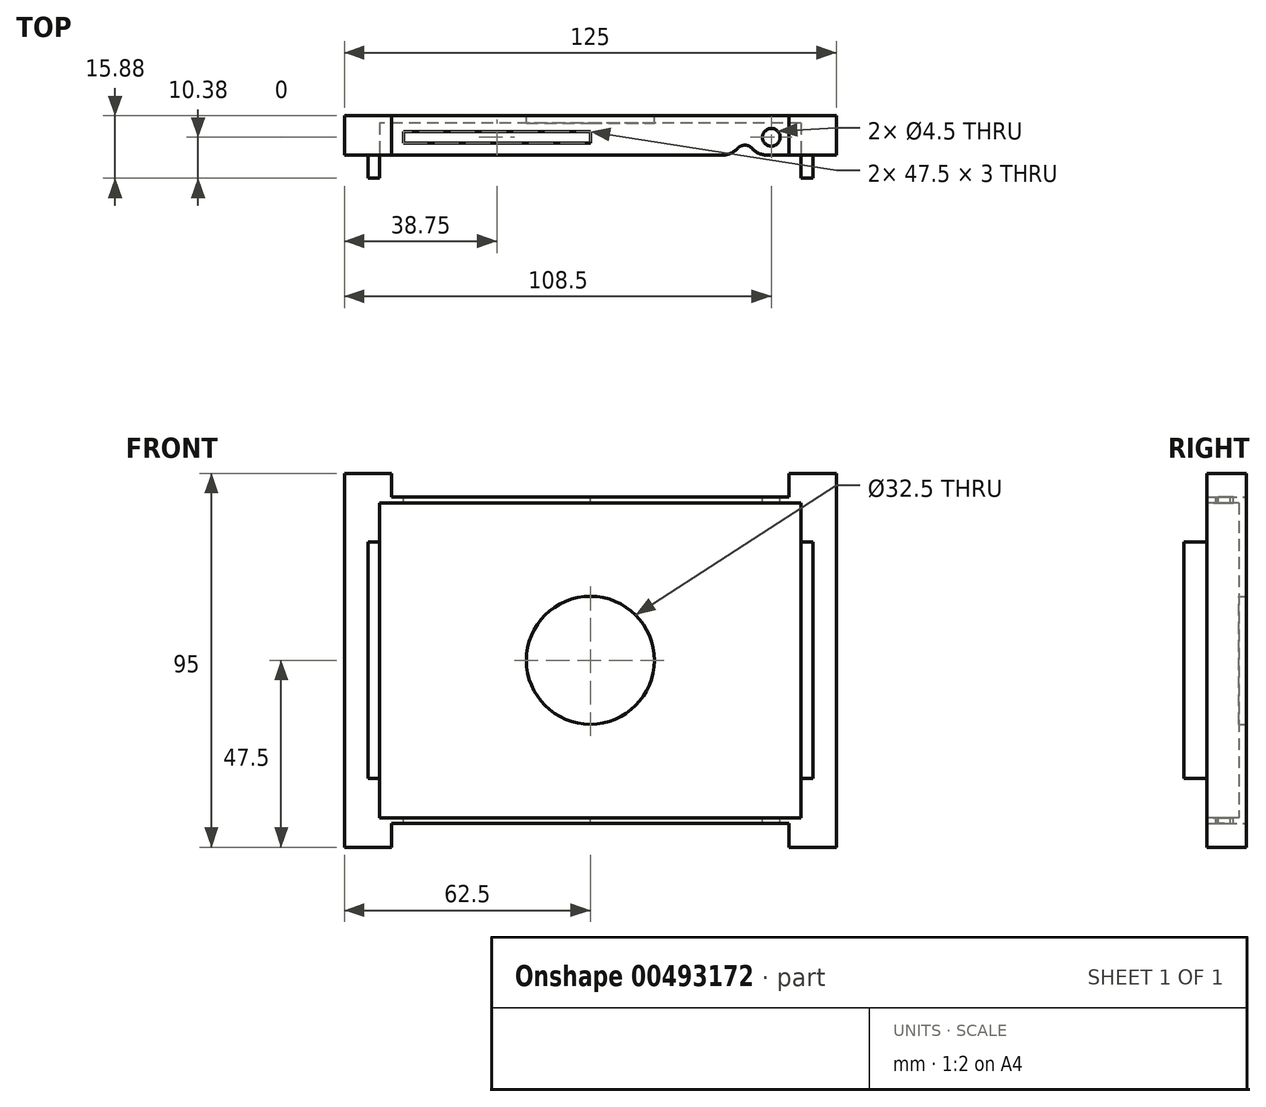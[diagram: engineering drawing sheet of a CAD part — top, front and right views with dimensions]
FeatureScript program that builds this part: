
annotation { "Feature Type Name" : "Feature", "Feature Type Description" : "" }
export const myFeature = defineFeature(function(context is Context, id is Id, definition is map)
    precondition{}
    {
        {
            var Q0;
            Q0=qCreatedBy(makeId("Front.planeOp"),FACE);
            var sketch = newSketch(context, id + "F0", { "sketchPlane" : qUnion([Q0])});
            skLineSegment(sketch, "E0.bottom", {"start": v(62.5, 47.5) * mm, "end": v(-62.5, 47.5) * mm, "construction": true});
            skLineSegment(sketch, "E0.top", {"start": v(62.5, -47.5) * mm, "end": v(-62.5, -47.5) * mm, "construction": true});
            skLineSegment(sketch, "E0.left", {"start": v(62.5, 47.5) * mm, "end": v(62.5, -47.5) * mm, "construction": true});
            skLineSegment(sketch, "E0.right", {"start": v(-62.5, 47.5) * mm, "end": v(-62.5, -47.5) * mm, "construction": true});
            skPoint(sketch, "E0.middle", {"position": v(0, 0) * mm});
            skLineSegment(sketch, "E1", {"start": v(-62.5, 47.5) * mm, "end": v(-50.5, 47.5) * mm});
            skLineSegment(sketch, "E2", {"start": v(62.5, 47.5) * mm, "end": v(50.5, 47.5) * mm});
            skLineSegment(sketch, "E3", {"start": v(50.5, 47.5) * mm, "end": v(50.5, 41.5) * mm});
            skLineSegment(sketch, "E4", {"start": v(50.5, 41.5) * mm, "end": v(-50.5, 41.5) * mm});
            skLineSegment(sketch, "E5", {"start": v(-50.5, 41.5) * mm, "end": v(-50.5, 47.5) * mm});
            skLineSegment(sketch, "E6", {"start": v(62.5, 47.5) * mm, "end": v(62.5, -47.5) * mm});
            skLineSegment(sketch, "E7", {"start": v(-62.5, -47.5) * mm, "end": v(-62.5, 47.5) * mm});
            skLineSegment(sketch, "E8", {"start": v(62.5, -47.5) * mm, "end": v(50.5, -47.5) * mm});
            skLineSegment(sketch, "E9", {"start": v(50.5, -47.5) * mm, "end": v(50.5, -41.5) * mm});
            skLineSegment(sketch, "E10", {"start": v(50.5, -41.5) * mm, "end": v(-50.5, -41.5) * mm});
            skLineSegment(sketch, "E11", {"start": v(-50.5, -41.5) * mm, "end": v(-50.5, -47.5) * mm});
            skLineSegment(sketch, "E12", {"start": v(-50.5, -47.5) * mm, "end": v(-62.5, -47.5) * mm});
            skCircle(sketch, "E13", {"center": v(0, 0) * mm, "radius": 16.25 * mm});
            skSolve(sketch);
        }
        {
            var Q0;
            Q0=qSketchRegion(id+"F0",true);
            extrude(context, id + "F1", {"entities" : qUnion([Q0]), "depth" : 15.88 * mm});
        }
        {
            var Q0;
            Q0=makeQuery(id+"F1.opExtrude","CAP_FACE",FACE,{"disambiguationData":[OSD([sQuery(id+"F0.wireOp",EDGE,"E1"),sQuery(id+"F0.wireOp",EDGE,"E2"),sQuery(id+"F0.wireOp",EDGE,"E3"),sQuery(id+"F0.wireOp",EDGE,"E4"),sQuery(id+"F0.wireOp",EDGE,"E5"),sQuery(id+"F0.wireOp",EDGE,"E6"),sQuery(id+"F0.wireOp",EDGE,"E7"),sQuery(id+"F0.wireOp",EDGE,"E8"),sQuery(id+"F0.wireOp",EDGE,"E9"),sQuery(id+"F0.wireOp",EDGE,"E10"),sQuery(id+"F0.wireOp",EDGE,"E11"),sQuery(id+"F0.wireOp",EDGE,"E12"),sQuery(id+"F0.wireOp",EDGE,"E13")])],"isStart":false});
            var sketch = newSketch(context, id + "F2", { "sketchPlane" : qUnion([Q0])});
            skLineSegment(sketch, "E14.bottom", {"start": v(56.5, 40) * mm, "end": v(-56.5, 40) * mm});
            skLineSegment(sketch, "E14.top", {"start": v(56.5, -40) * mm, "end": v(-56.5, -40) * mm});
            skLineSegment(sketch, "E14.left", {"start": v(56.5, 40) * mm, "end": v(56.5, -40) * mm});
            skLineSegment(sketch, "E14.right", {"start": v(-56.5, 40) * mm, "end": v(-56.5, -40) * mm});
            skPoint(sketch, "E14.middle", {"position": v(0, 0) * mm});
            skLineSegment(sketch, "E15.bottom", {"start": v(69.6, 57.77) * mm, "end": v(-69.6, 57.77) * mm});
            skLineSegment(sketch, "E15.top", {"start": v(69.6, -57.77) * mm, "end": v(-69.6, -57.77) * mm});
            skLineSegment(sketch, "E15.left", {"start": v(69.6, 57.77) * mm, "end": v(69.6, -57.77) * mm});
            skLineSegment(sketch, "E15.right", {"start": v(-69.6, 57.77) * mm, "end": v(-69.6, -57.77) * mm});
            skSolve(sketch);
        }
        {
            var Q0;
            Q0=qSketchRegion(id+"F2",true);
            extrude(context, id + "F3", {"entities" : qUnion([Q0]), "operationType" : NewBodyOperationType.REMOVE, "oppositeDirection" : true, "depth" : 5.88 * mm});
        }
        {
            var Q0;
            Q0=makeQuery(id+"F1.opExtrude","CAP_FACE",FACE,{"disambiguationData":[OSD([sQuery(id+"F0.wireOp",EDGE,"E1"),sQuery(id+"F0.wireOp",EDGE,"E2"),sQuery(id+"F0.wireOp",EDGE,"E3"),sQuery(id+"F0.wireOp",EDGE,"E4"),sQuery(id+"F0.wireOp",EDGE,"E5"),sQuery(id+"F0.wireOp",EDGE,"E6"),sQuery(id+"F0.wireOp",EDGE,"E7"),sQuery(id+"F0.wireOp",EDGE,"E8"),sQuery(id+"F0.wireOp",EDGE,"E9"),sQuery(id+"F0.wireOp",EDGE,"E10"),sQuery(id+"F0.wireOp",EDGE,"E11"),sQuery(id+"F0.wireOp",EDGE,"E12"),sQuery(id+"F0.wireOp",EDGE,"E13")])],"isStart":false});
            var sketch = newSketch(context, id + "F4", { "sketchPlane" : qUnion([Q0])});
            skLineSegment(sketch, "E16.bottom", {"start": v(53.5, 40) * mm, "end": v(-53.5, 40) * mm});
            skLineSegment(sketch, "E16.top", {"start": v(53.5, -40) * mm, "end": v(-53.5, -40) * mm});
            skLineSegment(sketch, "E16.left", {"start": v(53.5, 40) * mm, "end": v(53.5, -40) * mm});
            skLineSegment(sketch, "E16.right", {"start": v(-53.5, 40) * mm, "end": v(-53.5, -40) * mm});
            skPoint(sketch, "E16.middle", {"position": v(0, 0) * mm});
            skSolve(sketch);
        }
        {
            var Q0;
            Q0=qSketchRegion(id+"F4",true);
            extrude(context, id + "F5", {"entities" : qUnion([Q0]), "operationType" : NewBodyOperationType.REMOVE, "oppositeDirection" : true, "depth" : 14 * mm});
        }
        {
            var Q0;
            Q0=makeQuery(id+"F5.boolean.opBoolean","SPLIT",FACE,{"disambiguationData":[TD([makeQuery(id+"F3.boolean.opBoolean","COPY",FACE,{"derivedFrom":makeQuery(id+"F3.opExtrude","SWEPT_FACE",FACE,{"disambiguationData":[OSD([sQuery(id+"F2.wireOp",EDGE,"E14.right")])]})})])],"derivedFrom":makeQuery(id+"F1.opExtrude","CAP_FACE",FACE,{"disambiguationData":[OSD([sQuery(id+"F0.wireOp",EDGE,"E1"),sQuery(id+"F0.wireOp",EDGE,"E2"),sQuery(id+"F0.wireOp",EDGE,"E3"),sQuery(id+"F0.wireOp",EDGE,"E4"),sQuery(id+"F0.wireOp",EDGE,"E5"),sQuery(id+"F0.wireOp",EDGE,"E6"),sQuery(id+"F0.wireOp",EDGE,"E7"),sQuery(id+"F0.wireOp",EDGE,"E8"),sQuery(id+"F0.wireOp",EDGE,"E9"),sQuery(id+"F0.wireOp",EDGE,"E10"),sQuery(id+"F0.wireOp",EDGE,"E11"),sQuery(id+"F0.wireOp",EDGE,"E12"),sQuery(id+"F0.wireOp",EDGE,"E13")])],"isStart":false})});
            var sketch = newSketch(context, id + "F6", { "sketchPlane" : qUnion([Q0])});
            skLineSegment(sketch, "E17.bottom", {"start": v(-60.23, 43.15) * mm, "end": v(60.36, 43.15) * mm});
            skLineSegment(sketch, "E17.top", {"start": v(-60.23, 30) * mm, "end": v(60.36, 30) * mm});
            skLineSegment(sketch, "E17.left", {"start": v(-60.23, 43.15) * mm, "end": v(-60.23, 30) * mm});
            skLineSegment(sketch, "E17.right", {"start": v(60.36, 43.15) * mm, "end": v(60.36, 30) * mm});
            skLineSegment(sketch, "E18.bottom", {"start": v(-59.64, -45.81) * mm, "end": v(61.69, -45.81) * mm});
            skLineSegment(sketch, "E18.top", {"start": v(-59.64, -30) * mm, "end": v(61.69, -30) * mm});
            skLineSegment(sketch, "E18.left", {"start": v(-59.64, -45.81) * mm, "end": v(-59.64, -30) * mm});
            skLineSegment(sketch, "E18.right", {"start": v(61.69, -45.81) * mm, "end": v(61.69, -30) * mm});
            skSolve(sketch);
        }
        {
            var Q0;
            Q0=qSketchRegion(id+"F6",true);
            extrude(context, id + "F7", {"entities" : qUnion([Q0]), "operationType" : NewBodyOperationType.REMOVE, "oppositeDirection" : true, "depth" : 5.88 * mm});
        }
        {
            var Q0;
            Q0=makeQuery(id+"F1.opExtrude","SWEPT_FACE",FACE,{"disambiguationData":[OSD([sQuery(id+"F0.wireOp",EDGE,"E4")])]});
            var sketch = newSketch(context, id + "F8", { "sketchPlane" : qUnion([Q0])});
            skCircle(sketch, "E19", {"center": v(46, -5.5) * mm, "radius": 1.5 * mm});
            skLineSegment(sketch, "E20.bottom", {"start": v(41.5, -4) * mm, "end": v(-47.5, -4) * mm});
            skLineSegment(sketch, "E20.top", {"start": v(41.5, -7) * mm, "end": v(-47.5, -7) * mm});
            skLineSegment(sketch, "E20.left", {"start": v(41.5, -4) * mm, "end": v(41.5, -7) * mm});
            skLineSegment(sketch, "E20.right", {"start": v(-47.5, -4) * mm, "end": v(-47.5, -7) * mm});
            skSolve(sketch);
        }
        {
            var Q0;
            Q0=qSketchRegion(id+"F8",true);
            extrude(context, id + "F9", {"entities" : qUnion([Q0]), "operationType" : NewBodyOperationType.REMOVE, "oppositeDirection" : true, "depth" : 100 * mm});
        }
        {
            var Q0;
            Q0=makeQuery(id+"F1.opExtrude","SWEPT_FACE",FACE,{"disambiguationData":[OSD([sQuery(id+"F0.wireOp",EDGE,"E4")])]});
            var sketch = newSketch(context, id + "F10", { "sketchPlane" : qUnion([Q0])});
            skLineSegment(sketch, "E21.bottom", {"start": v(0, 0) * mm, "end": v(42.44, 0) * mm});
            skLineSegment(sketch, "E21.top", {"start": v(0, -10) * mm, "end": v(42.44, -10) * mm});
            skLineSegment(sketch, "E21.left", {"start": v(0, 0) * mm, "end": v(0, -10) * mm});
            skLineSegment(sketch, "E21.right", {"start": v(42.44, 0) * mm, "end": v(42.44, -10) * mm});
            skSolve(sketch);
        }
        {
            var Q0;
            Q0=qSketchRegion(id+"F10",true);
            extrude(context, id + "F11", {"entities" : qUnion([Q0]), "operationType" : NewBodyOperationType.ADD, "oppositeDirection" : true, "depth" : 1.5 * mm});
        }
        {
            var Q0;
            Q0=makeQuery(id+"F1.opExtrude","SWEPT_FACE",FACE,{"disambiguationData":[OSD([sQuery(id+"F0.wireOp",EDGE,"E10")])]});
            var sketch = newSketch(context, id + "F12", { "sketchPlane" : qUnion([Q0])});
            skLineSegment(sketch, "E22.bottom", {"start": v(0, 10) * mm, "end": v(42.52, 10) * mm});
            skLineSegment(sketch, "E22.top", {"start": v(0, 0) * mm, "end": v(42.52, 0) * mm});
            skLineSegment(sketch, "E22.left", {"start": v(0, 10) * mm, "end": v(0, 0) * mm});
            skLineSegment(sketch, "E22.right", {"start": v(42.52, 10) * mm, "end": v(42.52, 0) * mm});
            skSolve(sketch);
        }
        {
            var Q0;
            Q0=qSketchRegion(id+"F12",true);
            extrude(context, id + "F13", {"entities" : qUnion([Q0]), "operationType" : NewBodyOperationType.ADD, "oppositeDirection" : true, "depth" : 1.5 * mm});
        }
        {
            var Q0;
            Q0=makeQuery(id+"F13.boolean.opBoolean","MERGE",FACE,{"derivedFrom":[makeQuery(id+"F1.opExtrude","SWEPT_FACE",FACE,{"disambiguationData":[OSD([sQuery(id+"F0.wireOp",EDGE,"E10")])]}),makeQuery(id+"F13.opExtrude","CAP_FACE",FACE,{"disambiguationData":[OSD([sQuery(id+"F12.wireOp",EDGE,"E22.bottom"),sQuery(id+"F12.wireOp",EDGE,"E22.top"),sQuery(id+"F12.wireOp",EDGE,"E22.left"),sQuery(id+"F12.wireOp",EDGE,"E22.right")])],"isStart":true})]});
            var sketch = newSketch(context, id + "F14", { "sketchPlane" : qUnion([Q0])});
            skCircle(sketch, "E23", {"center": v(39.25, 10) * mm, "radius": 2.5 * mm});
            skSolve(sketch);
        }
        {
            var Q0;
            Q0=qSketchRegion(id+"F14",true);
            extrude(context, id + "F15", {"entities" : qUnion([Q0]), "operationType" : NewBodyOperationType.REMOVE, "oppositeDirection" : true, "depth" : 95.5 * mm});
        }
        {
            var Q0;
            Q0=makeQuery(id+"F11.boolean.opBoolean","MERGE",FACE,{"derivedFrom":[makeQuery(id+"F1.opExtrude","SWEPT_FACE",FACE,{"disambiguationData":[OSD([sQuery(id+"F0.wireOp",EDGE,"E4")])]}),makeQuery(id+"F11.opExtrude","CAP_FACE",FACE,{"disambiguationData":[OSD([sQuery(id+"F10.wireOp",EDGE,"E21.bottom"),sQuery(id+"F10.wireOp",EDGE,"E21.top"),sQuery(id+"F10.wireOp",EDGE,"E21.left"),sQuery(id+"F10.wireOp",EDGE,"E21.right")])],"isStart":true})]});
            var sketch = newSketch(context, id + "F16", { "sketchPlane" : qUnion([Q0])});
            skCircle(sketch, "E24", {"center": v(46, -5.5) * mm, "radius": 2.25 * mm});
            skSolve(sketch);
        }
        {
            var Q0;
            Q0=qSketchRegion(id+"F16",true);
            extrude(context, id + "F17", {"entities" : qUnion([Q0]), "operationType" : NewBodyOperationType.REMOVE, "oppositeDirection" : true, "depth" : 200 * mm});
        }
        {
            var Q0;
            Q0=makeQuery(id+"F15.boolean.opBoolean","INTERSECT",EDGE,{"disambiguationData":[OD(3.0)],"derivedFrom":[makeQuery(id+"F7.boolean.opBoolean","MERGE",FACE,{"derivedFrom":[makeQuery(id+"F3.boolean.opBoolean","COPY",FACE,{"derivedFrom":makeQuery(id+"F3.opExtrude","CAP_FACE",FACE,{"disambiguationData":[OSD([sQuery(id+"F2.wireOp",EDGE,"E14.bottom"),sQuery(id+"F2.wireOp",EDGE,"E14.top"),sQuery(id+"F2.wireOp",EDGE,"E14.left"),sQuery(id+"F2.wireOp",EDGE,"E14.right"),sQuery(id+"F2.wireOp",EDGE,"E15.bottom"),sQuery(id+"F2.wireOp",EDGE,"E15.top"),sQuery(id+"F2.wireOp",EDGE,"E15.left"),sQuery(id+"F2.wireOp",EDGE,"E15.right")])],"isStart":false})}),makeQuery(id+"F7.opExtrude","CAP_FACE",FACE,{"disambiguationData":[OSD([sQuery(id+"F6.wireOp",EDGE,"E17.bottom"),sQuery(id+"F6.wireOp",EDGE,"E17.top"),sQuery(id+"F6.wireOp",EDGE,"E17.left"),sQuery(id+"F6.wireOp",EDGE,"E17.right")])],"isStart":false}),makeQuery(id+"F7.opExtrude","CAP_FACE",FACE,{"disambiguationData":[OSD([sQuery(id+"F6.wireOp",EDGE,"E18.bottom"),sQuery(id+"F6.wireOp",EDGE,"E18.top"),sQuery(id+"F6.wireOp",EDGE,"E18.left"),sQuery(id+"F6.wireOp",EDGE,"E18.right")])],"isStart":false})]}),makeQuery(id+"F15.opExtrude","SWEPT_FACE",FACE,{"disambiguationData":[OSD([sQuery(id+"F14.wireOp",EDGE,"E23")])]})]});
            var Q1;
            Q1=makeQuery(id+"F15.boolean.opBoolean","INTERSECT",EDGE,{"disambiguationData":[OD(2.0)],"derivedFrom":[makeQuery(id+"F7.boolean.opBoolean","MERGE",FACE,{"derivedFrom":[makeQuery(id+"F3.boolean.opBoolean","COPY",FACE,{"derivedFrom":makeQuery(id+"F3.opExtrude","CAP_FACE",FACE,{"disambiguationData":[OSD([sQuery(id+"F2.wireOp",EDGE,"E14.bottom"),sQuery(id+"F2.wireOp",EDGE,"E14.top"),sQuery(id+"F2.wireOp",EDGE,"E14.left"),sQuery(id+"F2.wireOp",EDGE,"E14.right"),sQuery(id+"F2.wireOp",EDGE,"E15.bottom"),sQuery(id+"F2.wireOp",EDGE,"E15.top"),sQuery(id+"F2.wireOp",EDGE,"E15.left"),sQuery(id+"F2.wireOp",EDGE,"E15.right")])],"isStart":false})}),makeQuery(id+"F7.opExtrude","CAP_FACE",FACE,{"disambiguationData":[OSD([sQuery(id+"F6.wireOp",EDGE,"E17.bottom"),sQuery(id+"F6.wireOp",EDGE,"E17.top"),sQuery(id+"F6.wireOp",EDGE,"E17.left"),sQuery(id+"F6.wireOp",EDGE,"E17.right")])],"isStart":false}),makeQuery(id+"F7.opExtrude","CAP_FACE",FACE,{"disambiguationData":[OSD([sQuery(id+"F6.wireOp",EDGE,"E18.bottom"),sQuery(id+"F6.wireOp",EDGE,"E18.top"),sQuery(id+"F6.wireOp",EDGE,"E18.left"),sQuery(id+"F6.wireOp",EDGE,"E18.right")])],"isStart":false})]}),makeQuery(id+"F15.opExtrude","SWEPT_FACE",FACE,{"disambiguationData":[OSD([sQuery(id+"F14.wireOp",EDGE,"E23")])]})]});
            fillet(context, id + "F18", {"entities" : qUnion([Q0, Q1]), "radius" : 5 * mm, "tangentPropagation" : true, "allowEdgeOverflow" : false});
        }
    });
